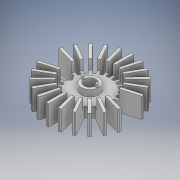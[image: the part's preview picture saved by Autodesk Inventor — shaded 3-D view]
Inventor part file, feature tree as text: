
AUTODESK INVENTOR PART (.ipt)
format: ipt  version: 2018 (Build 220112000, 112)  size: 385,024 bytes
history: native  units: mm
features: extrude x7, sketch x7
ambient origin geometry x8: Origin, YZ Plane, XZ Plane, XY Plane, X Axis, Y Axis, Z Axis, Center Point
bodies: Solid1 (feature_tree)
feature tree (14):
  extrude  "Extrusion1"  Depth=10.0mm TaperAngle=0.0deg
  extrude  "Extrusion2"  Depth=10.0mm TaperAngle=0.0deg
  extrude  "Extrusion3"  Depth=11.44mm
  extrude  "Extrusion4"  Depth=0.65mm
  extrude  "Extrusion6"  Depth=10.0mm TaperAngle=0.0deg
  extrude  "Extrusion9"  Depth=0.65mm
  extrude  "Extrusion10"  Depth=1.5mm
  sketch  "Sketch1"  dims[d0=19.91mm d1=10.0mm d2=0.0mm]
  sketch  "Sketch2"  dims[d3=2.43mm d4=2.43mm d5=10.0mm d6=0.0mm]
  sketch  "Sketch3"  dims[d7=42.0116mm d8=11.44mm]
  sketch  "Sketch4"  dims[d9=11.44mm d10=0.65mm]
  sketch  "Sketch6"  dims[d11=0.65mm d12=10.0mm d13=0.0mm]
  sketch  "Sketch10"  dims[d14=110.0mm d16=25.900686mm d18=0.65mm]
  sketch  "Sketch12"  dims[d19=0.65mm d20=110.0mm d22=25.900686mm d24=24.0mm d25=1.9mm d26=1.9mm d27=6.0mm d28=4.0mm d29=4.0mm d30=5.0mm d31=0.0mm d36=5.8mm d37=8.5mm d38=3.2mm d39=0.0mm d49=4.45mm d50=5.0mm d51=0.0mm d52=1.5mm d53=0.0mm]
